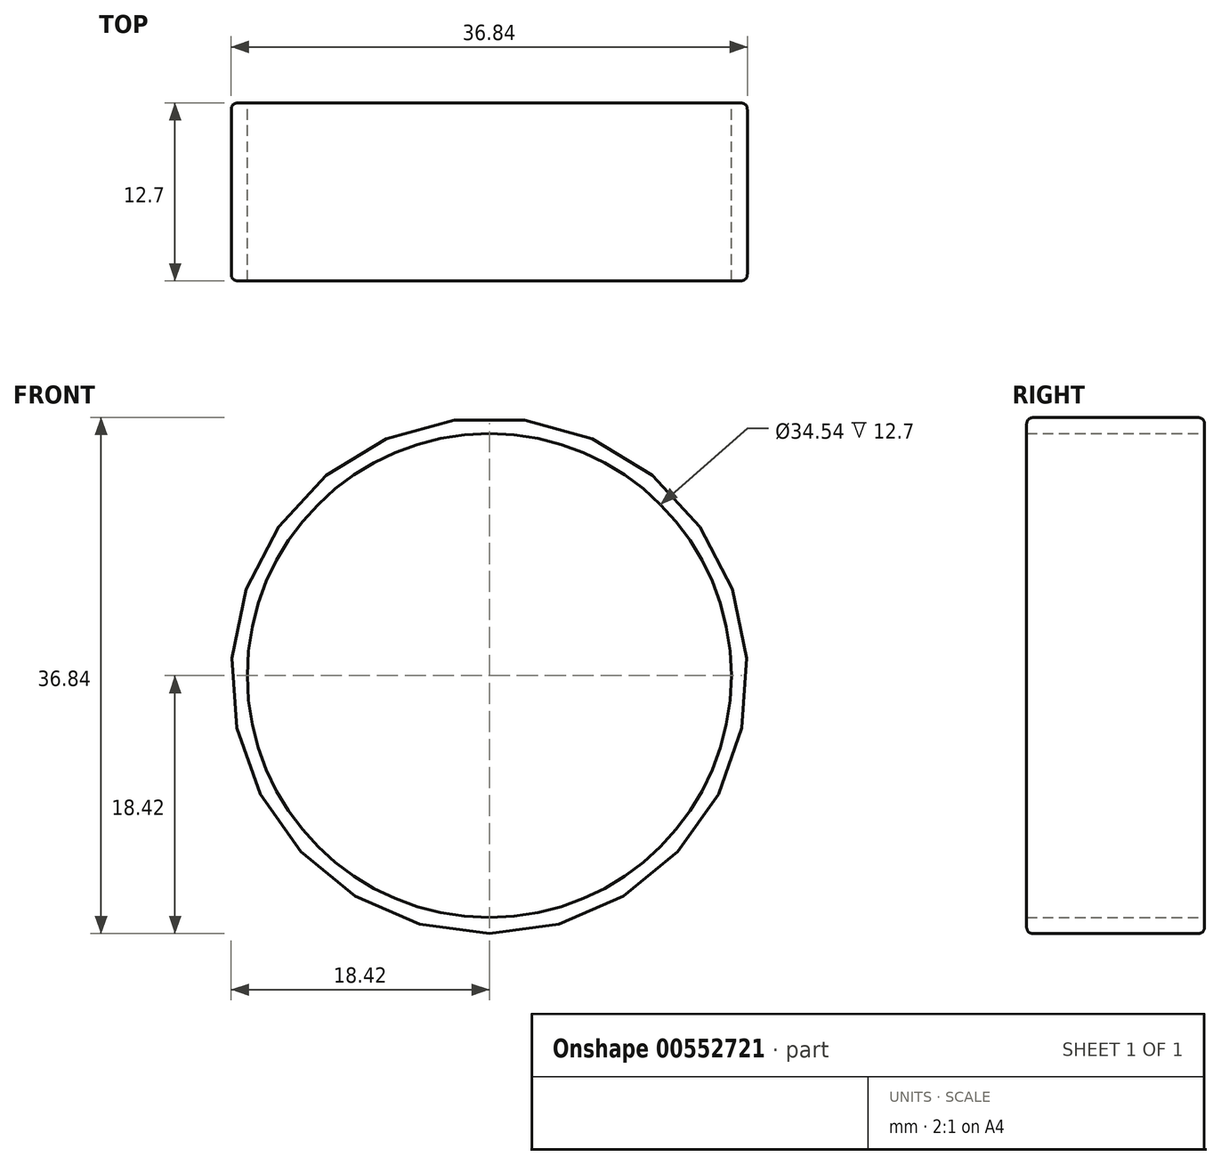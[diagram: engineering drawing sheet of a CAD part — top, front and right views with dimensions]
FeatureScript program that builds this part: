
annotation { "Feature Type Name" : "Feature", "Feature Type Description" : "" }
export const myFeature = defineFeature(function(context is Context, id is Id, definition is map)
    precondition{}
    {
        {
            var Q0;
            Q0=qCreatedBy(makeId("Front.planeOp"),FACE);
            var sketch = newSketch(context, id + "F0", { "sketchPlane" : qUnion([Q0])});
            skCircle(sketch, "E0", {"center": v(0, 0) * mm, "radius": 17.27 * mm});
            skCircle(sketch, "E1", {"center": v(0, 0) * mm, "radius": 18.41 * mm});
            skSolve(sketch);
        }
        {
            var Q0;
            Q0=qSketchRegion(id+"F0",true);
            extrude(context, id + "F1", {"entities" : qUnion([Q0]), "endBound" : BoundingType.SYMMETRIC, "depth" : 12.7 * mm, "offsetDistance" : 25.4 * mm});
        }
        {
            var Q0;
            Q0=makeQuery(id+"F1.opExtrude","SWEPT_FACE",FACE,{"disambiguationData":[OSD([sQuery(id+"F0.wireOp",EDGE,"E1")])]});
            fillet(context, id + "F2", {"entities" : qUnion([Q0]), "radius" : 0.5 * mm, "tangentPropagation" : true, "rho" : .5, "crossSection" : FilletCrossSection.CONIC, "allowEdgeOverflow" : false});
        }
    });
